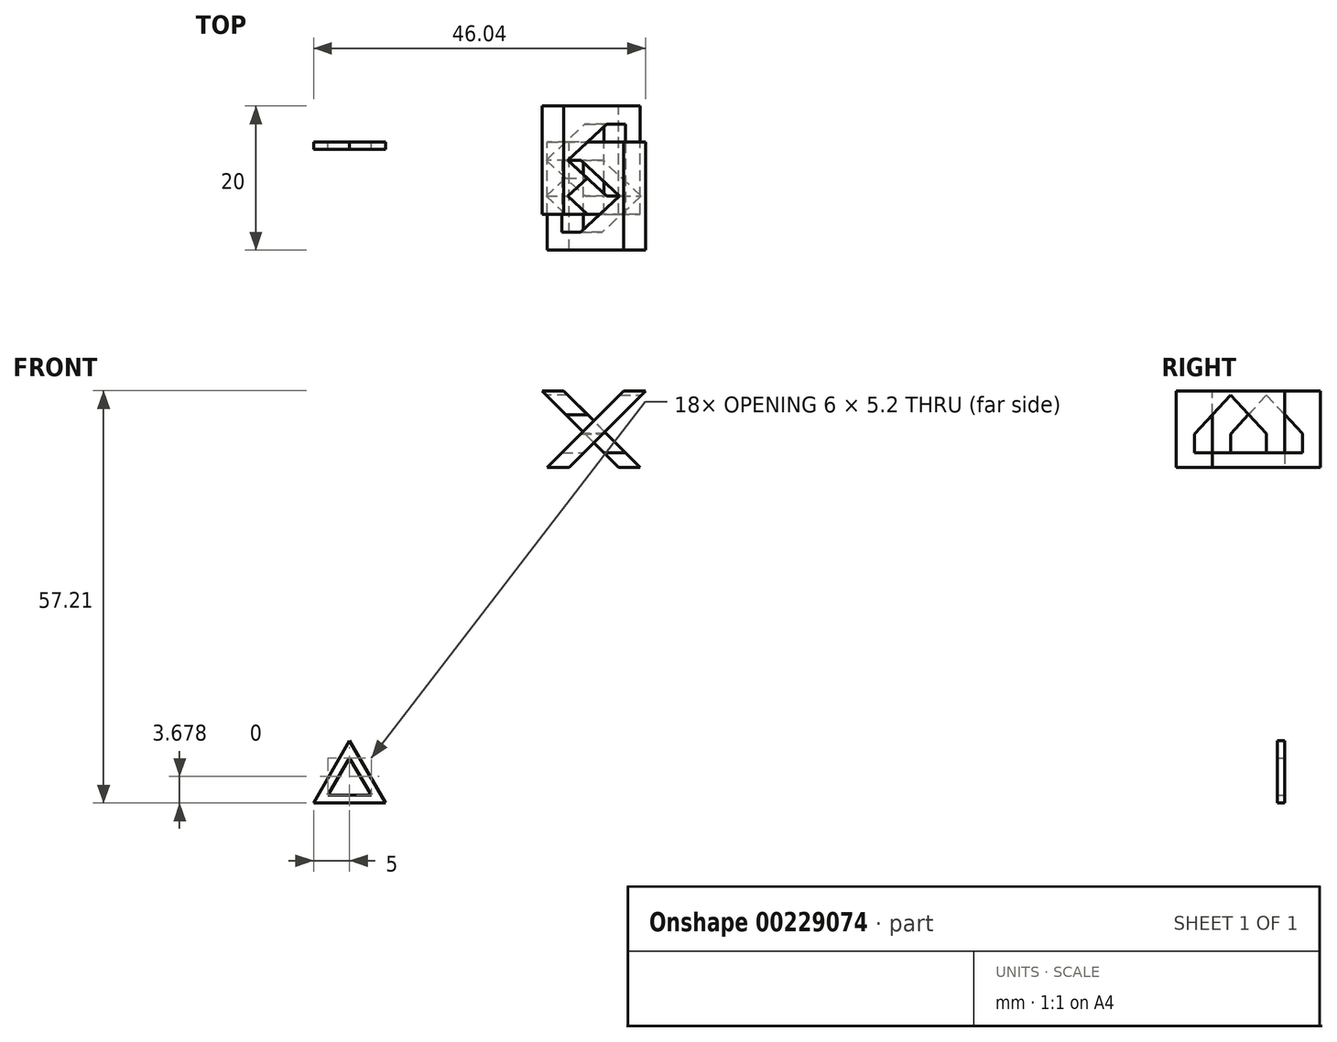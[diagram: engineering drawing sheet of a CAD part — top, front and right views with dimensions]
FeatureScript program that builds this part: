
annotation { "Feature Type Name" : "Feature", "Feature Type Description" : "" }
export const myFeature = defineFeature(function(context is Context, id is Id, definition is map)
    precondition{}
    {
        {
            var Q0;
            Q0=qCreatedBy(makeId("Front.planeOp"),FACE);
            var sketch = newSketch(context, id + "F0", { "sketchPlane" : qUnion([Q0])});
            skLineSegment(sketch, "E0", {"start": v(-65.86, -46.6) * mm, "end": v(-60.86, -37.94) * mm});
            skLineSegment(sketch, "E1", {"start": v(-60.86, -37.94) * mm, "end": v(-55.86, -46.6) * mm});
            skLineSegment(sketch, "E2", {"start": v(-55.86, -46.6) * mm, "end": v(-65.86, -46.6) * mm});
            skLineSegment(sketch, "E3", {"start": v(-60.86, -40.32) * mm, "end": v(-63.86, -45.52) * mm});
            skLineSegment(sketch, "E4", {"start": v(-63.86, -45.52) * mm, "end": v(-57.86, -45.52) * mm});
            skLineSegment(sketch, "E5", {"start": v(-57.86, -45.52) * mm, "end": v(-60.86, -40.32) * mm});
            skSolve(sketch);
        }
        {
            var Q0;
            Q0=makeQuery(id+"F0.imprint","IMPRINT",FACE,{"disambiguationData":[TD([[makeQuery(id+"F0.imprint","IMPRINT",EDGE,{"derivedFrom":sQuery(id+"F0.wireOp",EDGE,"E0")}),-1.0]])]});
            extrude(context, id + "F1", {"entities" : qUnion([Q0]), "depth" : 1 * mm});
        }
        {
            var Q0;
            Q0=qCreatedBy(makeId("Front.planeOp"),FACE);
            var sketch = newSketch(context, id + "F2", { "sketchPlane" : qUnion([Q0])});
            skLineSegment(sketch, "E6", {"start": v(-33.43, 0) * mm, "end": v(-22.82, 10.6) * mm});
            skLineSegment(sketch, "E7", {"start": v(-22.82, 10.6) * mm, "end": v(-19.82, 10.6) * mm});
            skLineSegment(sketch, "E8", {"start": v(-19.82, 10.6) * mm, "end": v(-30.43, 0) * mm});
            skLineSegment(sketch, "E9", {"start": v(-30.43, 0) * mm, "end": v(-33.43, 0) * mm});
            skSolve(sketch);
        }
        {
            var Q0;
            Q0=makeQuery(id+"F2.imprint","IMPRINT",FACE,{"disambiguationData":[TD([[makeQuery(id+"F2.imprint","IMPRINT",EDGE,{"derivedFrom":sQuery(id+"F2.wireOp",EDGE,"E6")}),-1.0]])]});
            extrude(context, id + "F3", {"entities" : qUnion([Q0]), "depth" : 15 * mm});
        }
        {
            var Q0;
            Q0=qCreatedBy(makeId("Right.planeOp"),FACE);
            var sketch = newSketch(context, id + "F4", { "sketchPlane" : qUnion([Q0])});
            skLineSegment(sketch, "E10.bottom", {"start": v(-12.5, 10) * mm, "end": v(-2.5, 10) * mm, "construction": true});
            skLineSegment(sketch, "E10.top", {"start": v(-12.5, 2) * mm, "end": v(-2.5, 2) * mm});
            skLineSegment(sketch, "E10.left", {"start": v(-12.5, 10) * mm, "end": v(-12.5, 2) * mm});
            skLineSegment(sketch, "E10.right", {"start": v(-2.5, 10) * mm, "end": v(-2.5, 2) * mm});
            skLineSegment(sketch, "E11", {"start": v(-7.5, 10) * mm, "end": v(-12.5, 4.6) * mm});
            skLineSegment(sketch, "E12", {"start": v(-7.5, 10) * mm, "end": v(-2.5, 4.65) * mm});
            skSolve(sketch);
        }
        {
            var Q0;
            Q0=qCreatedBy(makeId("Right.planeOp"),FACE);
            cPlane(context, id + "F5", {"entities" : qUnion([Q0]), "cplaneType" : CPlaneType.OFFSET, "offset" : 27 * mm, "oppositeDirection" : true, "width" : 150 * mm, "height" : 150 * mm});
        }
        {
            var Q0;
            {var subQ2=sQuery(id+"F4.wireOp",EDGE,"E10.top");Q0=makeQuery(id+"F4.imprint","IMPRINT",FACE,{"disambiguationData":[TD([[makeQuery(id+"F4.imprint","IMPRINT",EDGE,{"derivedFrom":subQ2}),1.0]])]});}
            var Q1;
            Q1=sQuery(id+"F4.wireOp",EDGE,"E10.bottom");
            var Q2;
            Q2=sQuery(id+"F4.wireOp",EDGE,"E10.top");
            var Q3;
            Q3=sQuery(id+"F4.wireOp",EDGE,"E10.left");
            var Q4;
            Q4=sQuery(id+"F4.wireOp",EDGE,"E11");
            var Q5;
            Q5=sQuery(id+"F4.wireOp",EDGE,"E12");
            var Q6;
            Q6=sQuery(id+"F4.wireOp",EDGE,"E10.right");
            extrude(context, id + "F6", {"entities" : qUnion([Q0]), "operationType" : NewBodyOperationType.REMOVE, "surfaceEntities" : qUnion([Q1, Q2, Q3, Q4, Q5, Q6]), "endBound" : BoundingType.THROUGH_ALL, "oppositeDirection" : true, "depth" : 25 * mm});
        }
        {
            var Q0;
            Q0=makeQuery(id+"F3.opExtrude","SWEPT_BODY",BODY,{"disambiguationData":[OSD([sQuery(id+"F2.wireOp",EDGE,"E6"),sQuery(id+"F2.wireOp",EDGE,"E7"),sQuery(id+"F2.wireOp",EDGE,"E8"),sQuery(id+"F2.wireOp",EDGE,"E9")])]});
            var Q1;
            Q1=qCreatedBy(id+"F5.planeOp",FACE);
            mirror(context, id + "F7", {"entities" : qUnion([Q0]), "mirrorPlane" : qUnion([Q1])});
        }
        {
            var Q0;
            Q0=makeQuery(id+"F7.opPattern","COPY",BODY,{"derivedFrom":makeQuery(id+"F3.opExtrude","SWEPT_BODY",BODY,{"disambiguationData":[OSD([sQuery(id+"F2.wireOp",EDGE,"E6"),sQuery(id+"F2.wireOp",EDGE,"E7"),sQuery(id+"F2.wireOp",EDGE,"E8"),sQuery(id+"F2.wireOp",EDGE,"E9")])]}),"instanceName":"1"});
            var Q1;
            Q1=makeQuery(id+"F3.opExtrude","SWEPT_EDGE",EDGE,{"disambiguationData":[OSD([sQuery(id+"F2.wireOp",EDGE,"E6"),sQuery(id+"F2.wireOp",EDGE,"E9")])]});
            transform(context, id + "F8", {"entities" : qUnion([Q0]), "transformType" : TransformType.TRANSLATION_DISTANCE, "transformDirection" : qUnion([Q1]), "distance" : 5 * mm, "makeCopy" : false});
        }
    });
